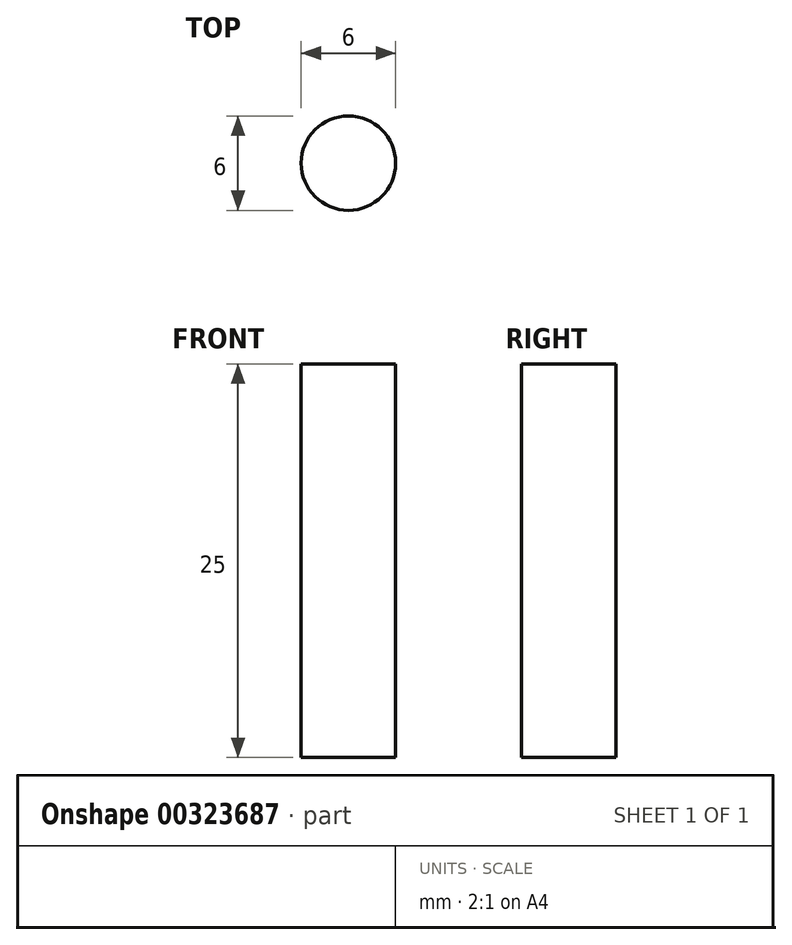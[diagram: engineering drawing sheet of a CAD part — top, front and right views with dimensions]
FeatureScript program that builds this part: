
annotation { "Feature Type Name" : "Feature", "Feature Type Description" : "" }
export const myFeature = defineFeature(function(context is Context, id is Id, definition is map)
    precondition{}
    {
        {
            var Q0;
            Q0=qCreatedBy(makeId("Top.planeOp"),FACE);
            var sketch = newSketch(context, id + "F0", { "sketchPlane" : qUnion([Q0])});
            skCircle(sketch, "E0", {"center": v(-35.33, -41.3) * mm, "radius": 3 * mm});
            skSolve(sketch);
        }
        {
            var Q0;
            Q0=makeQuery(id+"F0.imprint","IMPRINT",FACE,{"disambiguationData":[TD([[makeQuery(id+"F0.imprint","IMPRINT",EDGE,{"derivedFrom":sQuery(id+"F0.wireOp",EDGE,"E0")}),1.0]])]});
            extrude(context, id + "F1", {"entities" : qUnion([Q0]), "depth" : 25 * mm});
        }
    });
